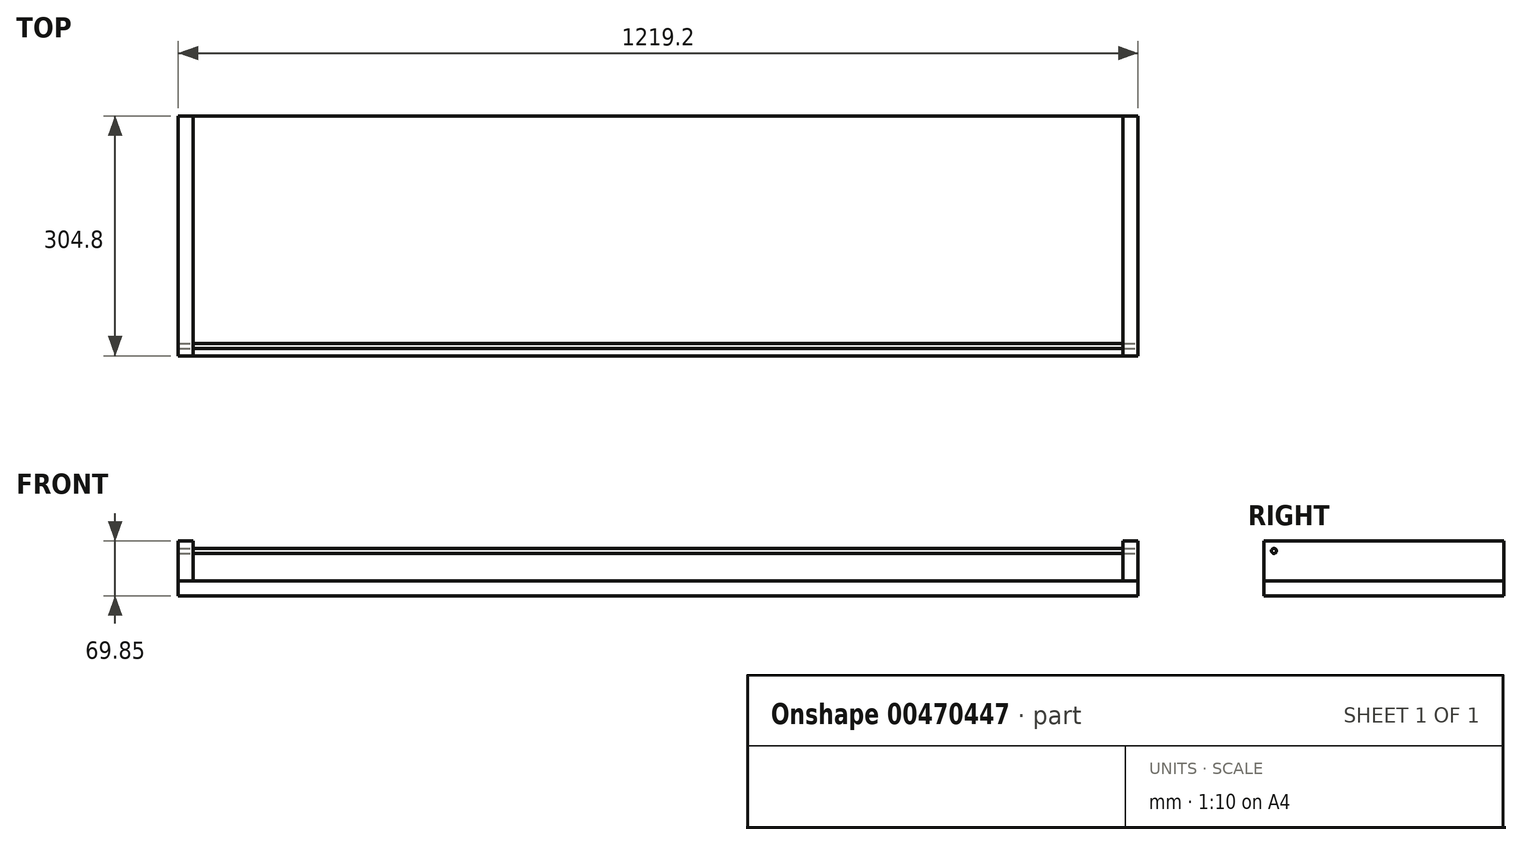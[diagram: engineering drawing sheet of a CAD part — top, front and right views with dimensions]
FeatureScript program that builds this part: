
annotation { "Feature Type Name" : "Feature", "Feature Type Description" : "" }
export const myFeature = defineFeature(function(context is Context, id is Id, definition is map)
    precondition{}
    {
        {
            var Q0;
            Q0=qCreatedBy(makeId("Top.planeOp"),FACE);
            var sketch = newSketch(context, id + "F0", { "sketchPlane" : qUnion([Q0])});
            skLineSegment(sketch, "E0.bottom", {"start": v(609.6, -152.4) * mm, "end": v(-609.6, -152.4) * mm});
            skLineSegment(sketch, "E0.top", {"start": v(609.6, 152.4) * mm, "end": v(-609.6, 152.4) * mm});
            skLineSegment(sketch, "E0.left", {"start": v(609.6, -152.4) * mm, "end": v(609.6, 152.4) * mm});
            skLineSegment(sketch, "E0.right", {"start": v(-609.6, -152.4) * mm, "end": v(-609.6, 152.4) * mm});
            skPoint(sketch, "E0.middle", {"position": v(0, 0) * mm});
            skSolve(sketch);
        }
        {
            var Q0;
            Q0 = qSketchRegion(id + "F0", true);
            extrude(context, id + "F1", {"entities" : qUnion([Q0]), "depth" : 19.05 * mm});
        }
        {
            var Q0;
            Q0=makeQuery(id+"F1.opExtrude","CAP_FACE",FACE,{"disambiguationData":[OSD([sQuery(id+"F0.wireOp",EDGE,"E0.bottom"),sQuery(id+"F0.wireOp",EDGE,"E0.top"),sQuery(id+"F0.wireOp",EDGE,"E0.left"),sQuery(id+"F0.wireOp",EDGE,"E0.right")])],"isStart":false});
            var sketch = newSketch(context, id + "F2", { "sketchPlane" : qUnion([Q0])});
            skLineSegment(sketch, "E1.bottom", {"start": v(-609.6, -152.4) * mm, "end": v(-590.55, -152.4) * mm});
            skLineSegment(sketch, "E1.top", {"start": v(-609.6, 152.4) * mm, "end": v(-590.55, 152.4) * mm});
            skLineSegment(sketch, "E1.left", {"start": v(-609.6, -152.4) * mm, "end": v(-609.6, 152.4) * mm});
            skLineSegment(sketch, "E1.right", {"start": v(-590.55, -152.4) * mm, "end": v(-590.55, 152.4) * mm});
            skSolve(sketch);
        }
        {
            var Q0;
            Q0 = qSketchRegion(id + "F2", true);
            extrude(context, id + "F3", {"entities" : qUnion([Q0]), "depth" : 50.8 * mm});
        }
        {
            var Q0;
            Q0=makeQuery(id+"F3.opExtrude","SWEPT_BODY",BODY,{"disambiguationData":[OSD([sQuery(id+"F2.wireOp",EDGE,"E1.bottom"),sQuery(id+"F2.wireOp",EDGE,"E1.top"),sQuery(id+"F2.wireOp",EDGE,"E1.left"),sQuery(id+"F2.wireOp",EDGE,"E1.right")])]});
            var Q1;
            Q1=qCreatedBy(makeId("Right.planeOp"),FACE);
            mirror(context, id + "F4", {"entities" : qUnion([Q0]), "mirrorPlane" : qUnion([Q1])});
        }
        {
            var Q0;
            Q0=makeQuery(id+"F4.opPattern","COPY",FACE,{"derivedFrom":makeQuery(id+"F3.opExtrude","SWEPT_FACE",FACE,{"disambiguationData":[OSD([sQuery(id+"F2.wireOp",EDGE,"E1.left")])]}),"instanceName":"1"});
            var sketch = newSketch(context, id + "F5", { "sketchPlane" : qUnion([Q0])});
            skCircle(sketch, "E2", {"center": v(-139.7, 57.15) * mm, "radius": 3.18 * mm});
            skSolve(sketch);
        }
        {
            var Q0;
            Q0 = qSketchRegion(id + "F5", true);
            var Q1;
            Q1=makeQuery(id+"F3.opExtrude","SWEPT_FACE",FACE,{"disambiguationData":[OSD([sQuery(id+"F2.wireOp",EDGE,"E1.left")])]});
            extrude(context, id + "F6", {"entities" : qUnion([Q0]), "endBound" : BoundingType.UP_TO_SURFACE, "oppositeDirection" : true, "endBoundEntityFace" : qUnion([Q1]), "depth" : 25.4 * mm});
        }
    });
